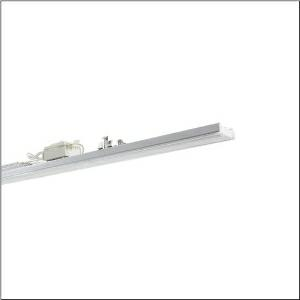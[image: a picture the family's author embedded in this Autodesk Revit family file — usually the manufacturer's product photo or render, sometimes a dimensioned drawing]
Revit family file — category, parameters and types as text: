
# Revit family: licross_r__21_recessed_mo_52te10cn49xg_034d
name_source: partatom
category: Lighting Fixtures
units: mm (PartAtom-declared; Revit-internal decimal feet)

## family parameters
Cut with Voids When Loaded = No
Host = Face
Light Source = No
Part Type = Normal
Room Calculation Point = No
Round Connector Dimension = Use Diameter
Shared = No

## types (1)
- --- (1 x LED, 9010 lm, 49.9 W, 4000K)
    Apparent Load = 50 VA
    CIE Flux Codes = 50 81 96 100 100
    Color Rendering = 80
    Color Temperature = 4000K
    Default Elevation = 1800 mm
    Description = Licross® 21 Recessed MO, luminaire insert, of sheet steel, galvanised, coil coated, white, length: 1.500mm, width: 66mm, height: 67mm, LED rated luminous flux: 9.010lm, light colour: 840, control gear: ON/OFF Multilumen, CLOi, control gear: ECG Multilumen, with plug, 3-pole, with phase selection, mains connection: 220..240V, AC, 50/60Hz, start of lifetime: 49W, end of service life: 61W, halogen-free wiring, primary optical cover: cover, of PMMA, light emission: direct distribution, primary light characteristic: symmetric, protection rating (complete): IP54, insulation class (complete): insulation class I (protective earthing), certification: CE, ENEC, VDE, UKCA, protection symbol: D if used in an environment with non-conductive dust loads with corresponding accessories, impact resistance: IK06, permissible ambient temperature for indoor applications: -35..+40°C, corresponds to IFS (International Featured Standards) requirements for safety and quality in the food industry, reducing of maximum allowable ambient temperature of 5°C with ceiling mounting, LABS conformity tested according to VDMA 24364:2018-05, packaging unit: 1 piece
    Height = 58 mm
    Lamp = 1 x LED
    Lamp Light Flux = 9010 lm
    Lamp Power = 49.9 W
    Lamp count = 1
    Length = 1500 mm
    Luminous efficacy = 181 lm/W
    Manufacturer = Siteco
    ModVariant = No
    Model = 52TE10CN49XG
    Mounting Place = Ceiling
    Mounting Type = Pendant
    Number of Poles = 1
    OnlyDefault = Yes
    Power Factor = 1
    Product Name = Licross® 21 Recessed MO
    Product group = luminaire insert
    ProductGroupID = 902
    Protection Class = Protection class I
    Protection Degree = IP 54
    RLX_Detail_Level = 1
    RLX_Emergency_Light_Flux = 0 lm
    RLX_Emergency_Type = 0
    RLX_Emergency_Type_DB = No
    RlxData = <blob elided: 22153 chars, md5=137a9c36>
    Socket = socket
    Standby Power = 0 W
    System Light Flux = 9010 lm
    System Power = 50 W
    Type Comments = factory setting: luminous flux: 100 % | (A | C | E) | 116 mA
    Type Image = l_1296930.jpg
    URL = http://relux.com
    VarID = @adj_110734
    Voltage = 0 V
    Weight = 0.00 kg
    Width = 66 mm

## geometry (parser evidence)
native form markers: Blend x4, Sweep x11
no freeform markers — native parametric forms only
